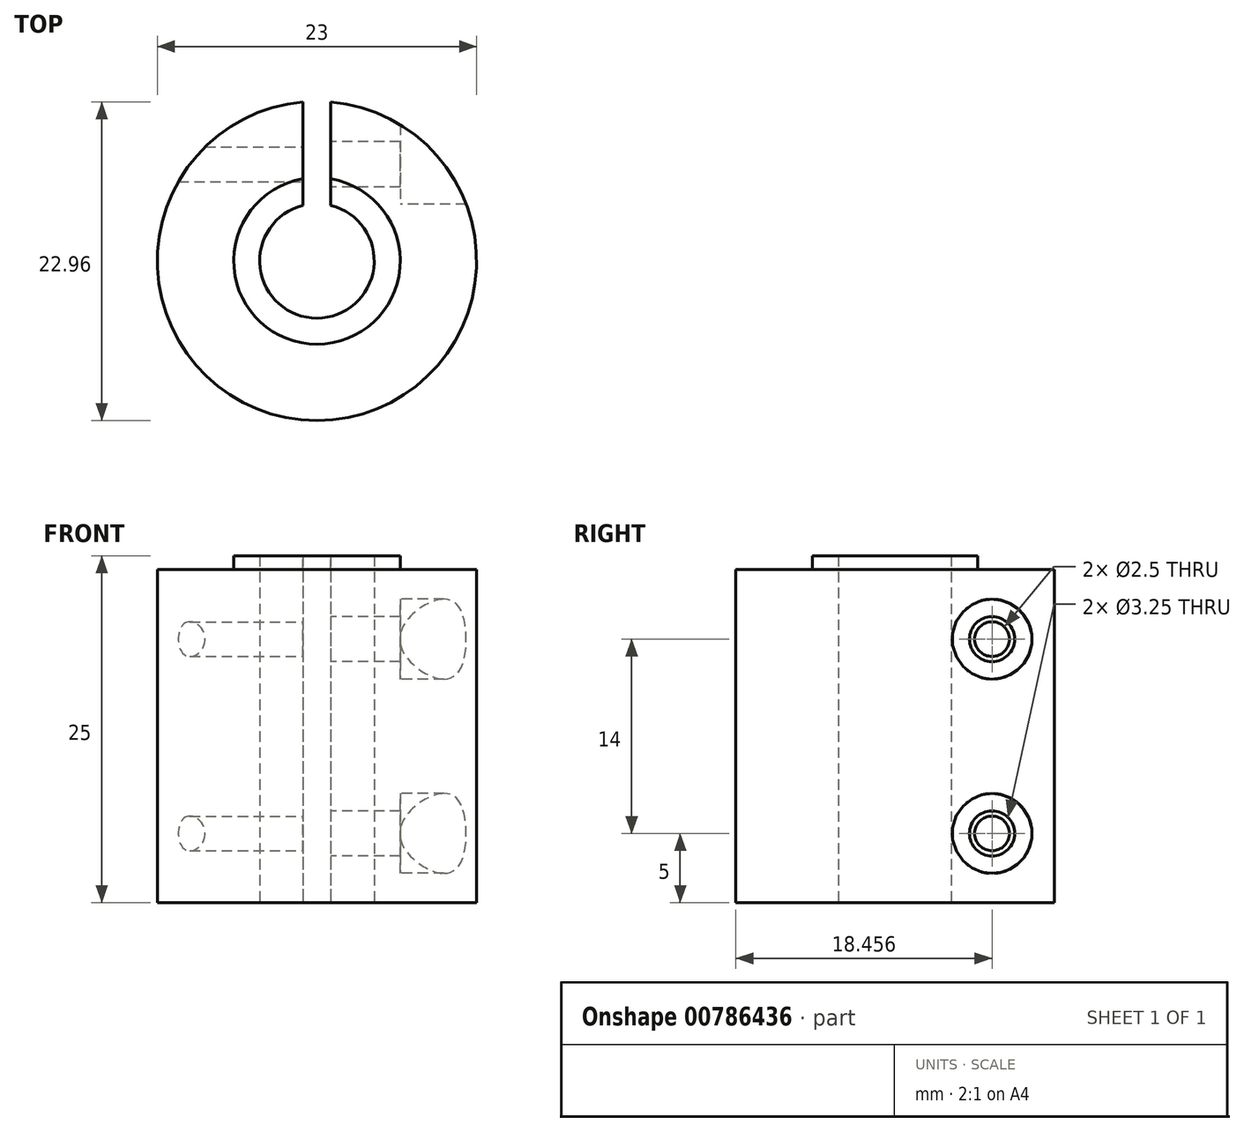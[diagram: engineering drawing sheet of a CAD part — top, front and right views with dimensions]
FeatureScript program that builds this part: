
annotation { "Feature Type Name" : "Feature", "Feature Type Description" : "" }
export const myFeature = defineFeature(function(context is Context, id is Id, definition is map)
    precondition{}
    {
        {
            var Q0;
            Q0=qCreatedBy(makeId("Top.planeOp"),FACE);
            var sketch = newSketch(context, id + "F0", { "sketchPlane" : qUnion([Q0])});
            skArc(sketch, "E0", {"start": v(-1, 4) * mm, "mid": v(0, -4.12) * mm, "end": v(1, 4) * mm});
            skArc(sketch, "E1", {"start": v(-1, 11.46) * mm, "mid": v(0, -11.5) * mm, "end": v(1, 11.46) * mm});
            skLineSegment(sketch, "E2", {"start": v(0, 15.2) * mm, "end": v(0, -16.59) * mm, "construction": true});
            skLineSegment(sketch, "E3", {"start": v(-1, 11.46) * mm, "end": v(-1, 4) * mm});
            skLineSegment(sketch, "E4", {"start": v(1, 11.46) * mm, "end": v(1, 4) * mm});
            skSolve(sketch);
        }
        {
            var Q0;
            Q0 = qSketchRegion(id + "F0", true);
            extrude(context, id + "F1", {"entities" : qUnion([Q0]), "depth" : 25 * mm, "offsetDistance" : 25 * mm});
        }
        {
            var Q0;
            Q0=makeQuery(id+"F1.opExtrude","CAP_FACE",FACE,{"disambiguationData":[OSD([sQuery(id+"F0.wireOp",EDGE,"E0"),sQuery(id+"F0.wireOp",EDGE,"E1"),sQuery(id+"F0.wireOp",EDGE,"E3"),sQuery(id+"F0.wireOp",EDGE,"E4")])],"isStart":false});
            var sketch = newSketch(context, id + "F2", { "sketchPlane" : qUnion([Q0])});
            skArc(sketch, "E5.0", {"start": v(-1, 11.46) * mm, "mid": v(0, -11.5) * mm, "end": v(1, 11.46) * mm});
            skArc(sketch, "E6", {"start": v(-1, 5.92) * mm, "mid": v(0, -6) * mm, "end": v(1, 5.92) * mm});
            skLineSegment(sketch, "E7.0", {"start": v(-1, 11.46) * mm, "end": v(-1, 5.92) * mm});
            skLineSegment(sketch, "E8.0", {"start": v(1, 11.46) * mm, "end": v(1, 5.92) * mm});
            skSolve(sketch);
        }
        {
            var Q0;
            Q0 = qSketchRegion(id + "F2", true);
            extrude(context, id + "F3", {"entities" : qUnion([Q0]), "operationType" : NewBodyOperationType.REMOVE, "oppositeDirection" : true, "depth" : 1 * mm, "offsetDistance" : 25 * mm});
        }
        {
            var Q0;
            Q0=makeQuery(id+"F1.opExtrude","SWEPT_FACE",FACE,{"disambiguationData":[OSD([sQuery(id+"F0.wireOp",EDGE,"E3")])]});
            var sketch = newSketch(context, id + "F4", { "sketchPlane" : qUnion([Q0])});
            skCircle(sketch, "E9", {"center": v(6.96, 19) * mm, "radius": 1.25 * mm});
            skCircle(sketch, "E10", {"center": v(6.96, 5) * mm, "radius": 1.25 * mm});
            skLineSegment(sketch, "E11", {"start": v(6.96, 31.19) * mm, "end": v(6.96, -8.4) * mm, "construction": true});
            skLineSegment(sketch, "E12", {"start": v(15.12, 12) * mm, "end": v(3.08, 12) * mm, "construction": true});
            skPoint(sketch, "E12.startSnap0", {"position": v(11.46, 12) * mm});
            skSolve(sketch);
        }
        {
            var Q0;
            Q0 = qSketchRegion(id + "F4", true);
            extrude(context, id + "F5", {"entities" : qUnion([Q0]), "operationType" : NewBodyOperationType.REMOVE, "endBound" : BoundingType.THROUGH_ALL, "oppositeDirection" : true, "depth" : 25 * mm, "offsetDistance" : 25 * mm});
        }
        {
            var Q0;
            Q0=makeQuery(id+"F1.opExtrude","SWEPT_FACE",FACE,{"disambiguationData":[OSD([sQuery(id+"F0.wireOp",EDGE,"E4")])]});
            var sketch = newSketch(context, id + "F6", { "sketchPlane" : qUnion([Q0])});
            skCircle(sketch, "E13", {"center": v(-6.96, 19) * mm, "radius": 1.63 * mm});
            skCircle(sketch, "E14", {"center": v(-6.96, 5) * mm, "radius": 1.63 * mm});
            skSolve(sketch);
        }
        {
            var Q0;
            Q0 = qSketchRegion(id + "F6", true);
            extrude(context, id + "F7", {"entities" : qUnion([Q0]), "operationType" : NewBodyOperationType.REMOVE, "endBound" : BoundingType.THROUGH_ALL, "oppositeDirection" : true, "depth" : 25 * mm, "offsetDistance" : 25 * mm});
        }
        {
            var Q0;
            Q0=makeQuery(id+"F1.opExtrude","SWEPT_FACE",FACE,{"disambiguationData":[OSD([sQuery(id+"F0.wireOp",EDGE,"E4")])]});
            cPlane(context, id + "F8", {"entities" : qUnion([Q0]), "cplaneType" : CPlaneType.OFFSET, "offset" : 5 * mm, "oppositeDirection" : true, "width" : 150 * mm, "height" : 150 * mm});
        }
        {
            var Q0;
            Q0=qCreatedBy(id+"F8.planeOp",FACE);
            var sketch = newSketch(context, id + "F9", { "sketchPlane" : qUnion([Q0])});
            skCircle(sketch, "E15", {"center": v(-6.96, 19) * mm, "radius": 2.88 * mm});
            skCircle(sketch, "E16", {"center": v(-6.96, 5) * mm, "radius": 2.88 * mm});
            skSolve(sketch);
        }
        {
            var Q0;
            Q0 = qSketchRegion(id + "F9", true);
            extrude(context, id + "F10", {"entities" : qUnion([Q0]), "operationType" : NewBodyOperationType.REMOVE, "endBound" : BoundingType.THROUGH_ALL, "oppositeDirection" : true, "depth" : 25 * mm, "offsetDistance" : 25 * mm});
        }
    });
